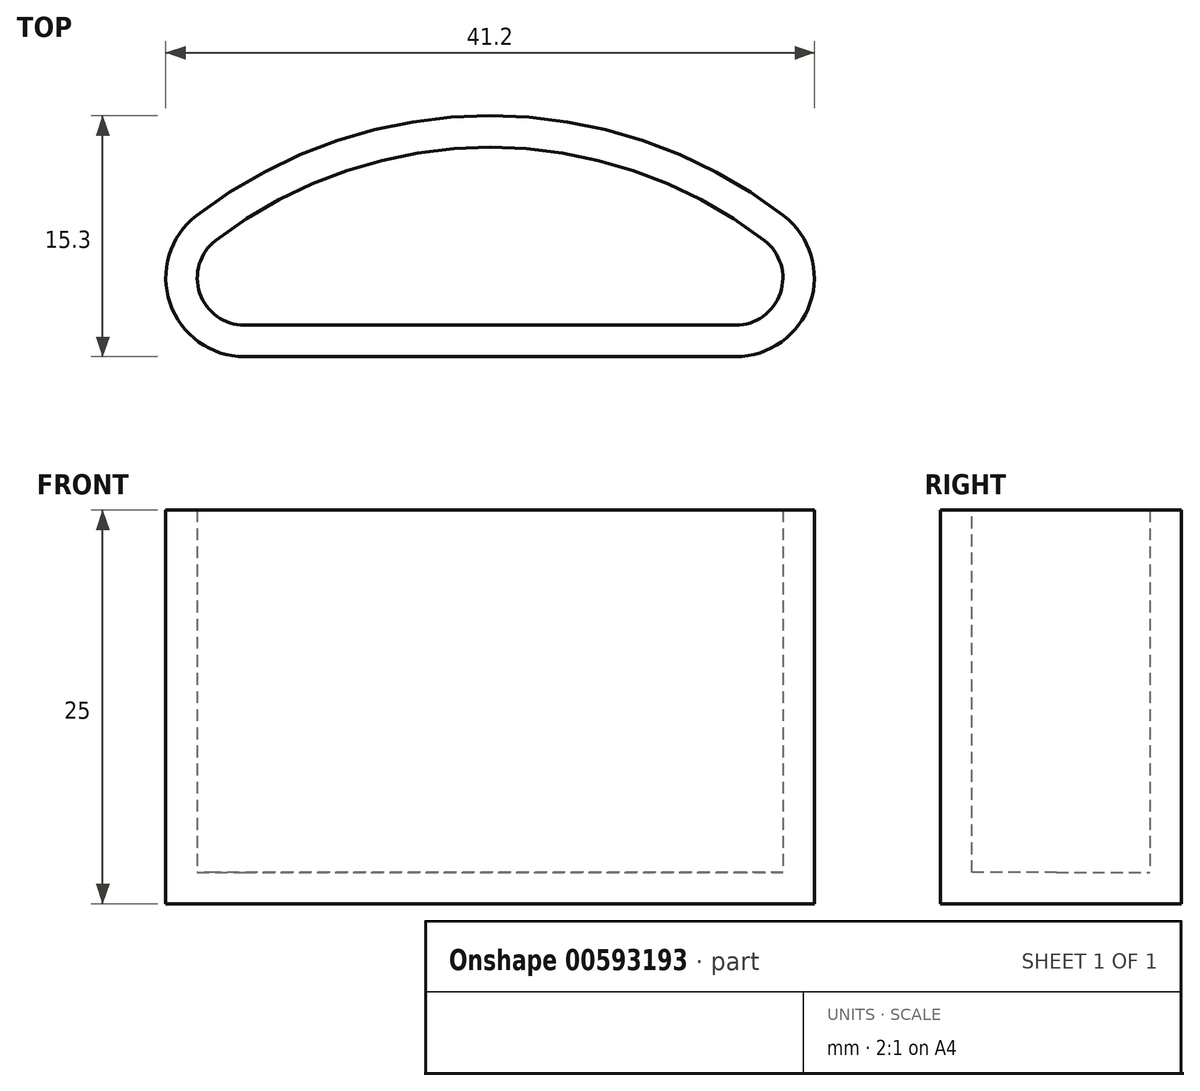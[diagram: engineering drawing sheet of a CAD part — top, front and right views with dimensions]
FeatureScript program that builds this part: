
annotation { "Feature Type Name" : "Feature", "Feature Type Description" : "" }
export const myFeature = defineFeature(function(context is Context, id is Id, definition is map)
    precondition{}
    {
        {
            var Q0;
            Q0=qCreatedBy(makeId("Top.planeOp"),FACE);
            var sketch = newSketch(context, id + "F0", { "sketchPlane" : qUnion([Q0])});
            skLineSegment(sketch, "E0", {"start": v(-26.5, 0) * mm, "end": v(26.5, 0) * mm});
            skCircle(sketch, "E1", {"center": v(0, -15.3) * mm, "radius": 30.6 * mm});
            skSolve(sketch);
        }
        {
            var Q0;
            {var subQ0=sQuery(id+"F0.wireOp",EDGE,"E0");Q0=makeQuery(id+"F0.imprint","IMPRINT",FACE,{"disambiguationData":[TD([[makeQuery(id+"F0.imprint","IMPRINT",EDGE,{"derivedFrom":subQ0}),1.0]])]});}
            extrude(context, id + "F1", {"entities" : qUnion([Q0]), "depth" : 25 * mm, "offsetDistance" : 25 * mm});
        }
        {
            var Q0;
            {var subQ0=sQuery(id+"F0.wireOp",EDGE,"E1");var subQ1=sQuery(id+"F0.wireOp",EDGE,"E0");Q0=makeQuery(id+"F1.opExtrude","SWEPT_EDGE",EDGE,{"disambiguationData":[OSD([subQ1,subQ0]),TDD([makeQuery(id+"F0.imprint","INTERSECT",VERTEX,{"disambiguationData":[OD(0.0)],"derivedFrom":[subQ1,subQ0]})])]});}
            var Q1;
            {var subQ0=sQuery(id+"F0.wireOp",EDGE,"E1");var subQ1=sQuery(id+"F0.wireOp",EDGE,"E0");Q1=makeQuery(id+"F1.opExtrude","SWEPT_EDGE",EDGE,{"disambiguationData":[OSD([subQ1,subQ0]),TDD([makeQuery(id+"F0.imprint","INTERSECT",VERTEX,{"disambiguationData":[OD(1.0)],"derivedFrom":[subQ1,subQ0]})])]});}
            fillet(context, id + "F2", {"entities" : qUnion([Q0, Q1]), "radius" : 5 * mm, "tangentPropagation" : true, "allowEdgeOverflow" : false});
        }
        {
            var Q0;
            Q0=makeQuery(id+"F1.opExtrude","CAP_FACE",FACE,{"disambiguationData":[OSD([sQuery(id+"F0.wireOp",EDGE,"E0"),sQuery(id+"F0.wireOp",EDGE,"E1")])],"isStart":false});
            var Q1;
            Q1=makeQuery(id+"F1.opExtrude","SWEPT_BODY",BODY,{"disambiguationData":[OSD([sQuery(id+"F0.wireOp",EDGE,"E0"),sQuery(id+"F0.wireOp",EDGE,"E1")])]});
            shell(context, id + "F3", {"entities" : qUnion([Q0]), "parts" : qUnion([Q1]), "thickness" : 2 * mm});
        }
    });
